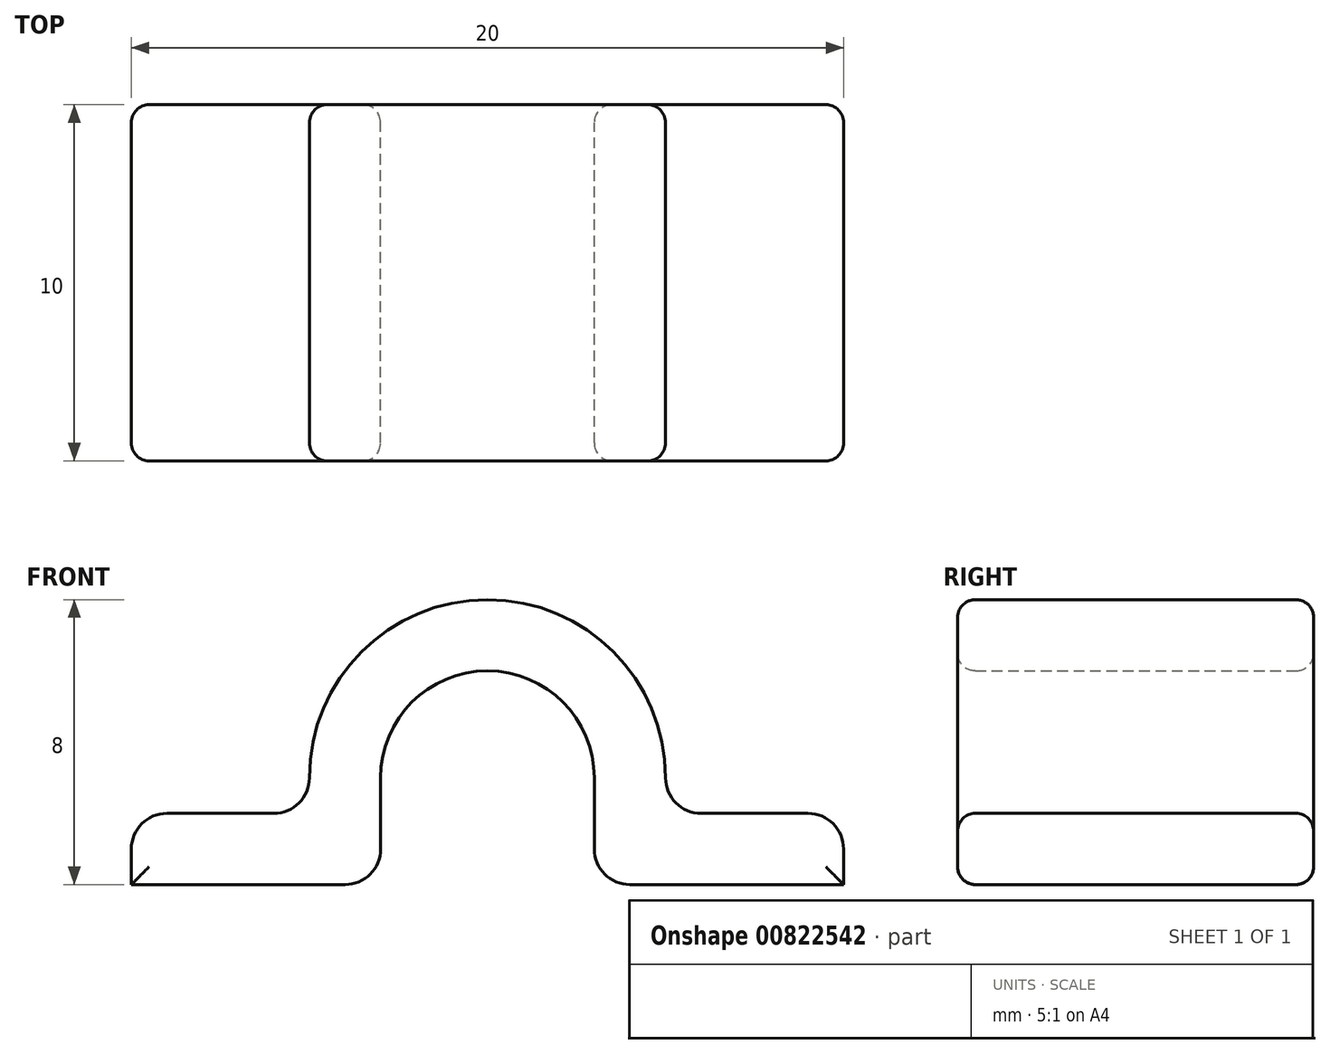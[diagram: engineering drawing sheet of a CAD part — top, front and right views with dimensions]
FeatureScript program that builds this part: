
annotation { "Feature Type Name" : "Feature", "Feature Type Description" : "" }
export const myFeature = defineFeature(function(context is Context, id is Id, definition is map)
    precondition{}
    {
        {
            var Q0;
            Q0=qCreatedBy(makeId("Front.planeOp"),FACE);
            var sketch = newSketch(context, id + "F0", { "sketchPlane" : qUnion([Q0])});
            skLineSegment(sketch, "E0", {"start": v(0, 0) * mm, "end": v(0, 6) * mm});
            skLineSegment(sketch, "E1", {"start": v(0, 6) * mm, "end": v(0, 8) * mm});
            skCircle(sketch, "E2", {"center": v(0, 3) * mm, "radius": 3 * mm});
            skCircle(sketch, "E3", {"center": v(0, 3) * mm, "radius": 5 * mm});
            skLineSegment(sketch, "E4", {"start": v(0, 3) * mm, "end": v(3, 3) * mm});
            skLineSegment(sketch, "E5", {"start": v(3, 3) * mm, "end": v(5, 3) * mm});
            skLineSegment(sketch, "E6", {"start": v(5, 3) * mm, "end": v(5, 3) * mm});
            skLineSegment(sketch, "E7", {"start": v(0, 0) * mm, "end": v(5, 0) * mm});
            skLineSegment(sketch, "E8", {"start": v(5, 0) * mm, "end": v(10, 0) * mm});
            skLineSegment(sketch, "E9", {"start": v(10, 0) * mm, "end": v(10, 2) * mm});
            skLineSegment(sketch, "E10", {"start": v(10, 2) * mm, "end": v(5, 2) * mm});
            skLineSegment(sketch, "E11", {"start": v(5, 2) * mm, "end": v(5, 3) * mm});
            skLineSegment(sketch, "E12", {"start": v(3, 3) * mm, "end": v(3, 0) * mm});
            skSolve(sketch);
        }
        {
            var Q0;
            {var subQ0=sQuery(id+"F0.wireOp",EDGE,"E8");Q0=makeQuery(id+"F0.imprint","IMPRINT",FACE,{"disambiguationData":[TD([[makeQuery(id+"F0.imprint","IMPRINT",EDGE,{"derivedFrom":subQ0}),1.0]])]});}
            var Q1;
            {var subQ0=sQuery(id+"F0.wireOp",EDGE,"E5");Q1=makeQuery(id+"F0.imprint","IMPRINT",FACE,{"disambiguationData":[TD([[makeQuery(id+"F0.imprint","IMPRINT",EDGE,{"derivedFrom":subQ0}),-1.0]])]});}
            var Q2;
            {var subQ0=sQuery(id+"F0.wireOp",EDGE,"E1");Q2=makeQuery(id+"F0.imprint","IMPRINT",FACE,{"disambiguationData":[TD([[makeQuery(id+"F0.imprint","IMPRINT",EDGE,{"derivedFrom":subQ0}),-1.0]])]});}
            extrude(context, id + "F1", {"entities" : qUnion([Q0, Q1, Q2]), "depth" : 10 * mm, "offsetDistance" : 25 * mm});
        }
        {
            var Q0;
            Q0=makeQuery(id+"F1.opExtrude","SWEPT_EDGE",EDGE,{"disambiguationData":[OSD([sQuery(id+"F0.wireOp",EDGE,"E10"),sQuery(id+"F0.wireOp",EDGE,"E11")])]});
            var Q1;
            Q1=makeQuery(id+"F1.opExtrude","SWEPT_EDGE",EDGE,{"disambiguationData":[OSD([sQuery(id+"F0.wireOp",EDGE,"E7"),sQuery(id+"F0.wireOp",EDGE,"E12")])]});
            var Q2;
            Q2=makeQuery(id+"F1.opExtrude","SWEPT_EDGE",EDGE,{"disambiguationData":[OSD([sQuery(id+"F0.wireOp",EDGE,"E9"),sQuery(id+"F0.wireOp",EDGE,"E10")])]});
            fillet(context, id + "F2", {"entities" : qUnion([Q0, Q1, Q2]), "radius" : 1 * mm, "tangentPropagation" : true, "allowEdgeOverflow" : false});
        }
        {
            var Q0;
            Q0=makeQuery(id+"F1.opExtrude","CAP_EDGE",EDGE,{"disambiguationData":[OSD([sQuery(id+"F0.wireOp",EDGE,"E2")])],"isStart":false});
            var Q1;
            Q1=makeQuery(id+"F1.opExtrude","CAP_EDGE",EDGE,{"disambiguationData":[OSD([sQuery(id+"F0.wireOp",EDGE,"E3")])],"isStart":false});
            var Q2;
            {var subQ0=sQuery(id+"F0.wireOp",EDGE,"E11");var subQ1=sQuery(id+"F0.wireOp",EDGE,"E10");Q2=makeQuery(id+"F2.opFillet","BLEND_EDGE",EDGE,{"blendedFrom":[makeQuery(id+"F1.opExtrude","SWEPT_EDGE",EDGE,{"disambiguationData":[OSD([subQ1,subQ0])]}),makeQuery(id+"F1.opExtrude","CAP_FACE",FACE,{"disambiguationData":[OSD([sQuery(id+"F0.wireOp",EDGE,"E1"),sQuery(id+"F0.wireOp",EDGE,"E2"),sQuery(id+"F0.wireOp",EDGE,"E3"),sQuery(id+"F0.wireOp",EDGE,"E7"),sQuery(id+"F0.wireOp",EDGE,"E8"),sQuery(id+"F0.wireOp",EDGE,"E9"),subQ1,subQ0,sQuery(id+"F0.wireOp",EDGE,"E12")])],"isStart":true})],"blendedInto":[makeQuery(id+"F1.opExtrude","CAP_FACE",FACE,{"disambiguationData":[OSD([sQuery(id+"F0.wireOp",EDGE,"E1"),sQuery(id+"F0.wireOp",EDGE,"E2"),sQuery(id+"F0.wireOp",EDGE,"E3"),sQuery(id+"F0.wireOp",EDGE,"E7"),sQuery(id+"F0.wireOp",EDGE,"E8"),sQuery(id+"F0.wireOp",EDGE,"E9"),subQ1,subQ0,sQuery(id+"F0.wireOp",EDGE,"E12")])],"isStart":true})]});}
            var Q3;
            Q3=makeQuery(id+"F1.opExtrude","CAP_EDGE",EDGE,{"disambiguationData":[OSD([sQuery(id+"F0.wireOp",EDGE,"E12")])],"isStart":true});
            fillet(context, id + "F3", {"entities" : qUnion([Q0, Q1, Q2, Q3]), "radius" : .5 * mm, "tangentPropagation" : true, "allowEdgeOverflow" : false});
        }
        {
            var Q0;
            Q0=makeQuery(id+"F1.opExtrude","SWEPT_BODY",BODY,{"disambiguationData":[OSD([sQuery(id+"F0.wireOp",EDGE,"E1"),sQuery(id+"F0.wireOp",EDGE,"E2"),sQuery(id+"F0.wireOp",EDGE,"E3"),sQuery(id+"F0.wireOp",EDGE,"E7"),sQuery(id+"F0.wireOp",EDGE,"E8"),sQuery(id+"F0.wireOp",EDGE,"E9"),sQuery(id+"F0.wireOp",EDGE,"E10"),sQuery(id+"F0.wireOp",EDGE,"E11"),sQuery(id+"F0.wireOp",EDGE,"E12")])]});
            var Q1;
            Q1=makeQuery(id+"F1.opExtrude","SWEPT_FACE",FACE,{"disambiguationData":[OSD([sQuery(id+"F0.wireOp",EDGE,"E1")])]});
            mirror(context, id + "F4", {"operationType" : NewBodyOperationType.ADD, "entities" : qUnion([Q0]), "mirrorPlane" : qUnion([Q1])});
        }
    });
